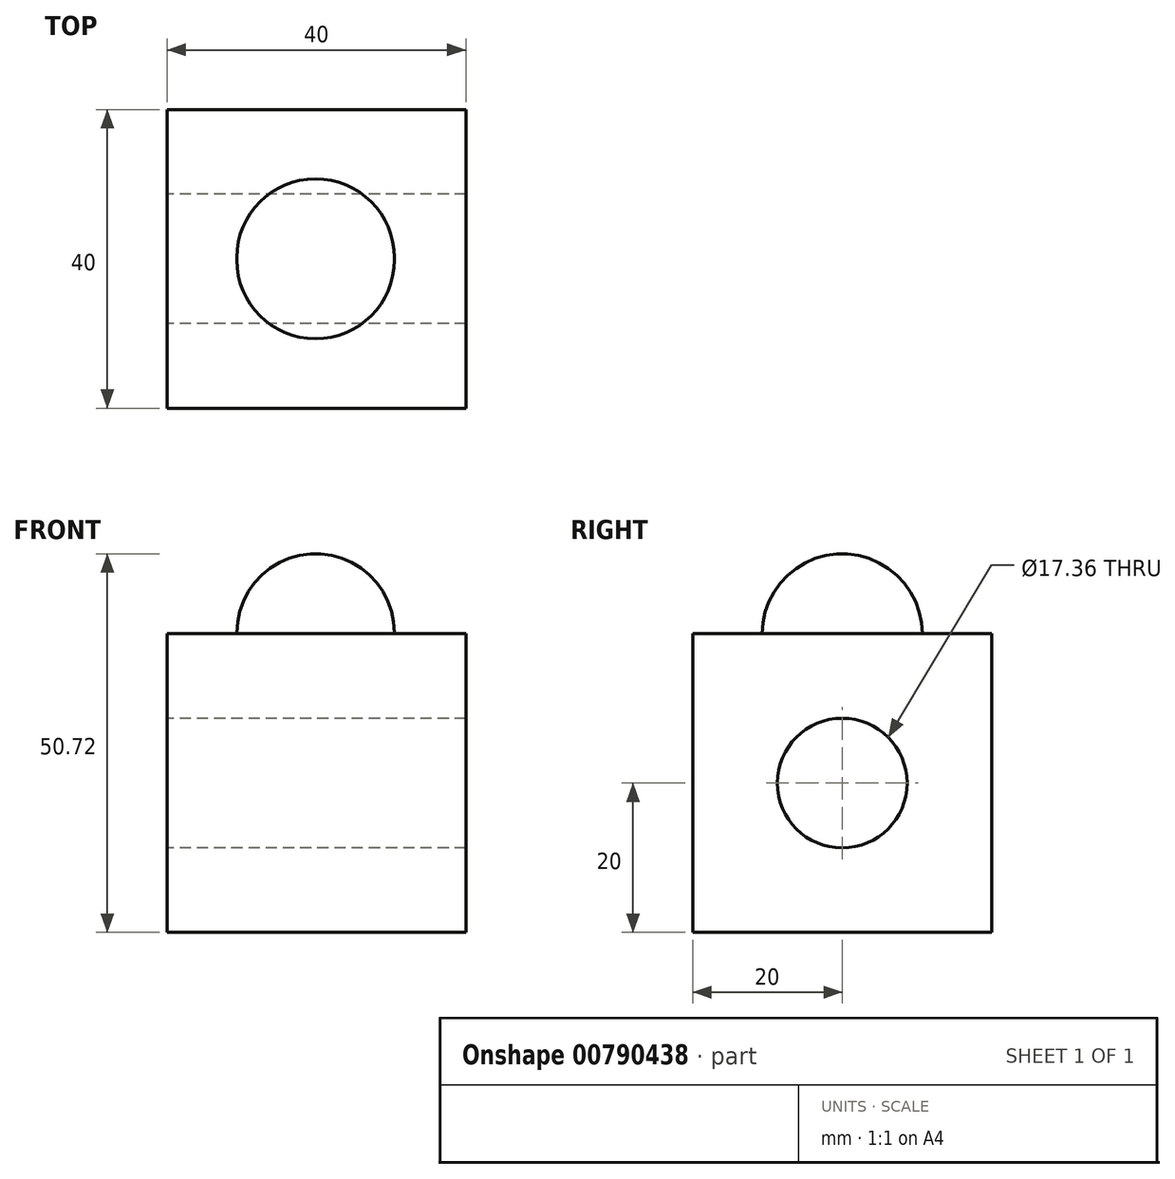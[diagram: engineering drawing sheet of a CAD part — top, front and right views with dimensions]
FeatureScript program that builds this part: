
annotation { "Feature Type Name" : "Feature", "Feature Type Description" : "" }
export const myFeature = defineFeature(function(context is Context, id is Id, definition is map)
    precondition{}
    {
        {
            var Q0;
            Q0=qCreatedBy(makeId("Front.planeOp"),FACE);
            var sketch = newSketch(context, id + "F0", { "sketchPlane" : qUnion([Q0])});
            skLineSegment(sketch, "E0.bottom", {"start": v(0, 0) * mm, "end": v(40, 0) * mm});
            skLineSegment(sketch, "E0.top", {"start": v(0, 40) * mm, "end": v(40, 40) * mm});
            skLineSegment(sketch, "E0.left", {"start": v(0, 0) * mm, "end": v(0, 40) * mm});
            skLineSegment(sketch, "E0.right", {"start": v(40, 0) * mm, "end": v(40, 40) * mm});
            skSolve(sketch);
        }
        {
            var Q0;
            Q0 = qSketchRegion(id + "F0", true);
            extrude(context, id + "F1", {"entities" : qUnion([Q0]), "depth" : 40 * mm, "offsetDistance" : 25 * mm});
        }
        {
            var Q0;
            Q0=makeQuery(id+"F1.opExtrude","SWEPT_FACE",FACE,{"disambiguationData":[OSD([sQuery(id+"F0.wireOp",EDGE,"E0.left")])]});
            var sketch = newSketch(context, id + "F2", { "sketchPlane" : qUnion([Q0])});
            skCircle(sketch, "E1", {"center": v(20, 20) * mm, "radius": 8.68 * mm});
            skPoint(sketch, "E1.centerSnap0", {"position": v(40, 20) * mm});
            skPoint(sketch, "E1.centerSnap1", {"position": v(20, 40) * mm});
            skSolve(sketch);
        }
        {
            var Q0;
            Q0=makeQuery(id+"F2.imprint","IMPRINT",FACE,{"disambiguationData":[TD([[makeQuery(id+"F2.imprint","IMPRINT",EDGE,{"derivedFrom":sQuery(id+"F2.wireOp",EDGE,"E1")}),1.0]])]});
            extrude(context, id + "F3", {"entities" : qUnion([Q0]), "operationType" : NewBodyOperationType.REMOVE, "oppositeDirection" : true, "depth" : 25 * mm, "offsetDistance" : 25 * mm});
        }
        {
            var Q0;
            Q0=makeQuery(id+"F3.boolean.opBoolean","COPY",FACE,{"derivedFrom":makeQuery(id+"F3.opExtrude","CAP_FACE",FACE,{"disambiguationData":[OSD([sQuery(id+"F2.wireOp",EDGE,"E1")])],"isStart":false})});
            extrude(context, id + "F4", {"entities" : qUnion([Q0]), "operationType" : NewBodyOperationType.REMOVE, "oppositeDirection" : true, "depth" : 40 * mm, "offsetDistance" : 25 * mm});
        }
        {
            var Q0;
            Q0=makeQuery(id+"F1.opExtrude","SWEPT_FACE",FACE,{"disambiguationData":[OSD([sQuery(id+"F0.wireOp",EDGE,"E0.top")])]});
            var sketch = newSketch(context, id + "F5", { "sketchPlane" : qUnion([Q0])});
            skLineSegment(sketch, "E2", {"start": v(30.41, -20) * mm, "end": v(9.34, -20) * mm});
            skPoint(sketch, "E2.startSnap0", {"position": v(40, -20) * mm});
            skLineSegment(sketch, "E3", {"start": v(9.34, -20) * mm, "end": v(14.94, -20) * mm});
            skArc(sketch, "E4", {"start": v(9.34, -20) * mm, "mid": v(19.88, -30.72) * mm, "end": v(30.41, -20) * mm});
            skSolve(sketch);
        }
        {
            var Q0;
            Q0 = qSketchRegion(id + "F5", true);
            var Q1;
            Q1=sQuery(id+"F5.wireOp",EDGE,"E2");
            revolve(context, id + "F6", {"operationType" : NewBodyOperationType.ADD, "surfaceOperationType" : NewSurfaceOperationType.NEW, "entities" : qUnion([Q0]), "axis" : qUnion([Q1]), "revolveType" : RevolveType.FULL});
        }
    });
